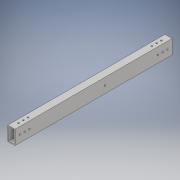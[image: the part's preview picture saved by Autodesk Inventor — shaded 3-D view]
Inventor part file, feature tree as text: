
AUTODESK INVENTOR PART (.ipt)
format: ipt  version: 2019 (Build 230136000, 136)  size: 177,664 bytes
history: native  units: mm
features: sketch x5, hole x3, extrude x2, other x1
ambient origin geometry x8: Origin, YZ Plane, XZ Plane, XY Plane, X Axis, Y Axis, Z Axis, Center Point
bodies: Body1 (feature_tree)
feature tree (11):
  other  "ソリッド1"
  extrude  "押し出し1"  Depth=15.0mm
  hole  "穴1"  [1 undecoded]
  hole  "穴2"  [1 undecoded]
  extrude  "押し出し2"  Depth=3.0mm
  hole  "穴3"  [1 undecoded]
  sketch  "スケッチ1"
  sketch  "スケッチ2"
  sketch  "スケッチ3"
  sketch  "スケッチ4"
  sketch  "スケッチ5"
note: 3 required parameter values undecoded (feature->parameter linkage not recoverable at this tier; creation-order binding heuristic only, values carry confidence <= 0.55)
